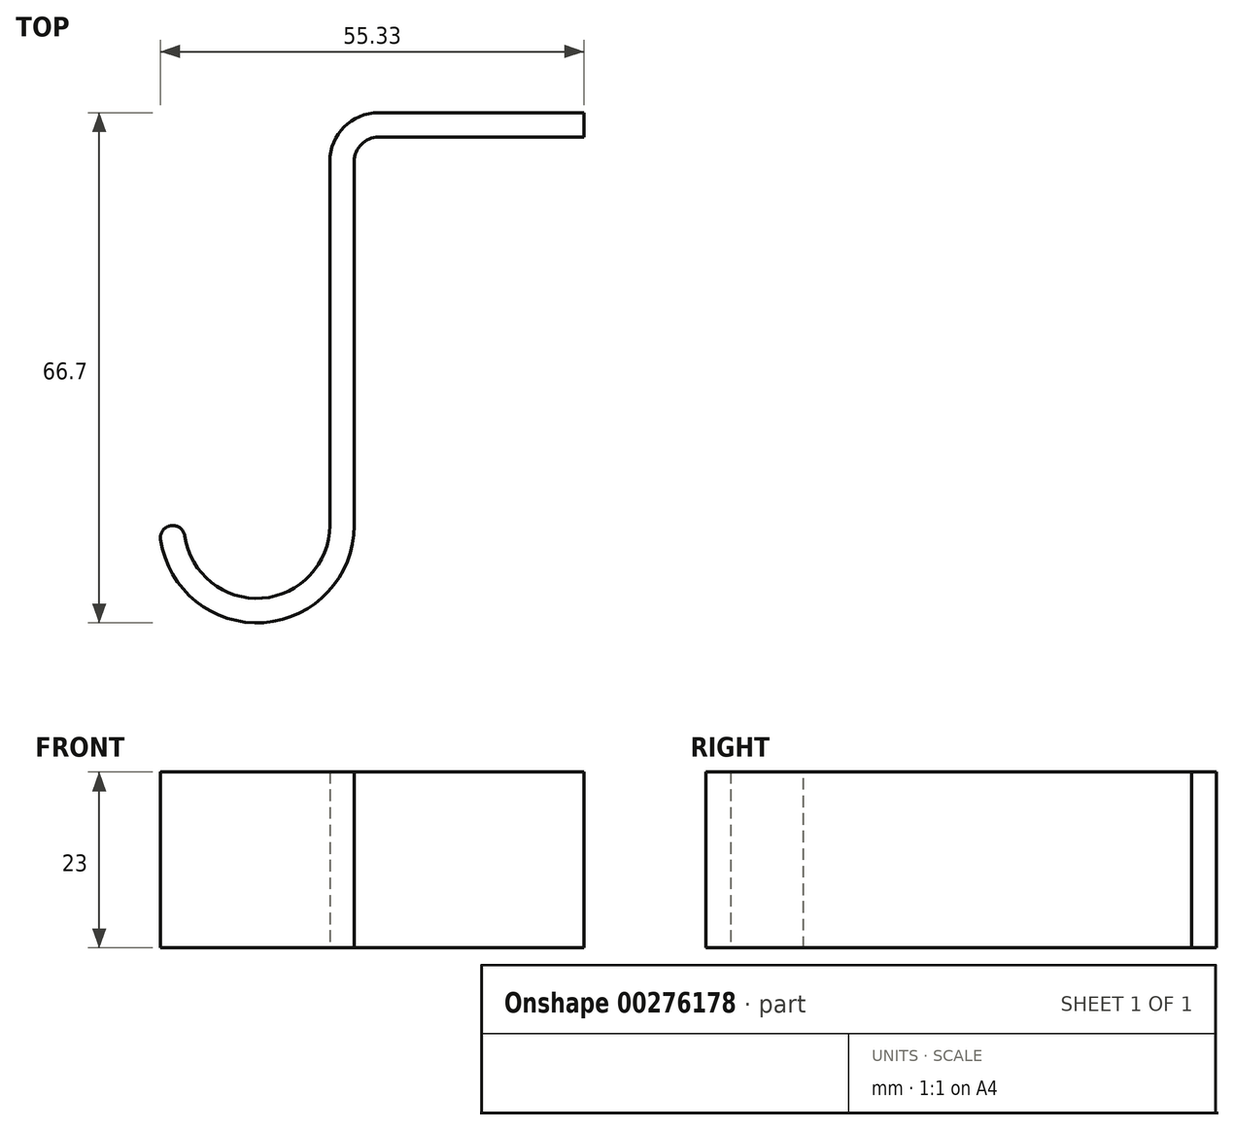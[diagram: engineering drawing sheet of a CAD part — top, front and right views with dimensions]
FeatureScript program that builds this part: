
annotation { "Feature Type Name" : "Feature", "Feature Type Description" : "" }
export const myFeature = defineFeature(function(context is Context, id is Id, definition is map)
    precondition{}
    {
        {
            var Q0;
            Q0=qCreatedBy(makeId("Top.planeOp"),FACE);
            var sketch = newSketch(context, id + "F0", { "sketchPlane" : qUnion([Q0])});
            skLineSegment(sketch, "E0", {"start": v(0, 0) * mm, "end": v(30, 0) * mm});
            skLineSegment(sketch, "E1", {"start": v(30, 0) * mm, "end": v(30, 3.2) * mm});
            skLineSegment(sketch, "E2", {"start": v(30, 3.2) * mm, "end": v(-3.2, 3.2) * mm});
            skLineSegment(sketch, "E3", {"start": v(-3.2, 3.2) * mm, "end": v(-3.2, -50.77) * mm});
            skLineSegment(sketch, "E4", {"start": v(0, 0) * mm, "end": v(0, -50.77) * mm});
            skArc(sketch, "E5", {"start": v(-25.45, -50.77) * mm, "mid": v(-12.72, -63.5) * mm, "end": v(0, -50.77) * mm});
            skArc(sketch, "E6", {"start": v(-22.25, -50.77) * mm, "mid": v(-12.73, -60.3) * mm, "end": v(-3.2, -50.78) * mm});
            skLineSegment(sketch, "E7", {"start": v(-22.25, -50.77) * mm, "end": v(-25.45, -50.77) * mm});
            skSolve(sketch);
        }
        {
            var Q0;
            Q0 = qSketchRegion(id + "F0", true);
            extrude(context, id + "F1", {"entities" : qUnion([Q0]), "depth" : 23 * mm});
        }
        {
            var Q0;
            Q0=makeQuery(id+"F1.opExtrude","SWEPT_EDGE",EDGE,{"disambiguationData":[OSD([sQuery(id+"F0.wireOp",EDGE,"E2"),sQuery(id+"F0.wireOp",EDGE,"E3")])]});
            fillet(context, id + "F2", {"entities" : qUnion([Q0]), "radius" : 3.2 * mm * 2, "tangentPropagation" : true, "allowEdgeOverflow" : false});
        }
        {
            var Q0;
            Q0=makeQuery(id+"F1.opExtrude","SWEPT_EDGE",EDGE,{"disambiguationData":[OSD([sQuery(id+"F0.wireOp",EDGE,"E0"),sQuery(id+"F0.wireOp",EDGE,"E4")])]});
            fillet(context, id + "F3", {"entities" : qUnion([Q0]), "radius" : 3.2 * mm, "tangentPropagation" : true, "allowEdgeOverflow" : false});
        }
        {
            var Q0;
            Q0=makeQuery(id+"F1.opExtrude","SWEPT_EDGE",EDGE,{"disambiguationData":[OSD([sQuery(id+"F0.wireOp",EDGE,"E5"),sQuery(id+"F0.wireOp",EDGE,"E7")])]});
            var Q1;
            Q1=makeQuery(id+"F1.opExtrude","SWEPT_EDGE",EDGE,{"disambiguationData":[OSD([sQuery(id+"F0.wireOp",EDGE,"E6"),sQuery(id+"F0.wireOp",EDGE,"E7")])]});
            fillet(context, id + "F4", {"entities" : qUnion([Q0, Q1]), "radius" : 1.6 * mm, "tangentPropagation" : true, "allowEdgeOverflow" : false});
        }
    });
